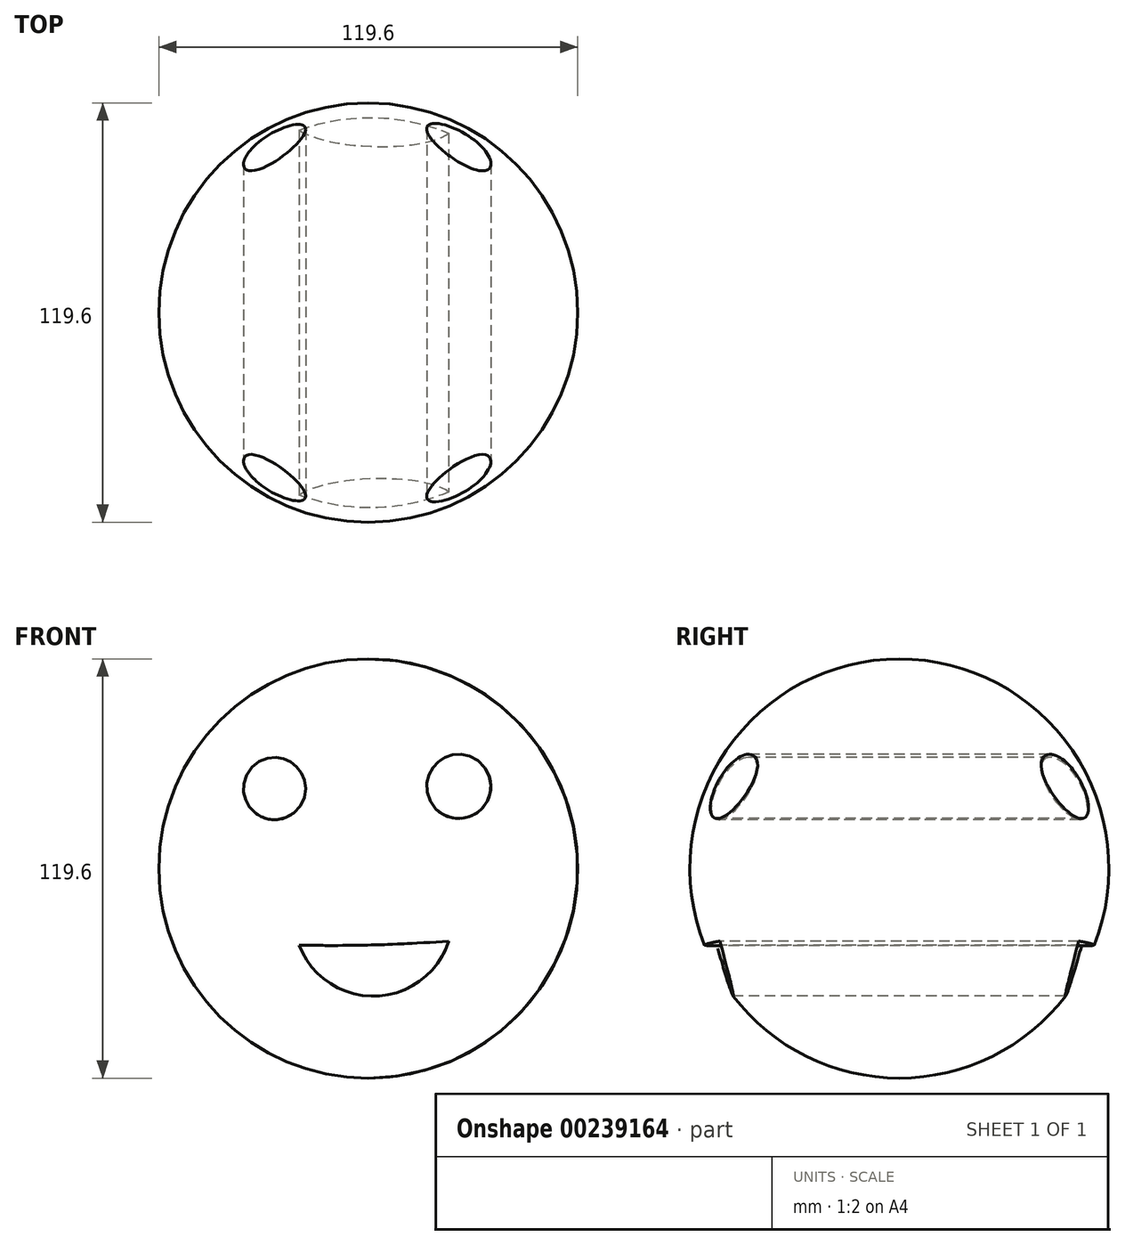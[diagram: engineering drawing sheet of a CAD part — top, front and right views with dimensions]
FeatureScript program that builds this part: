
annotation { "Feature Type Name" : "Feature", "Feature Type Description" : "" }
export const myFeature = defineFeature(function(context is Context, id is Id, definition is map)
    precondition{}
    {
        {
            var Q0;
            Q0=qCreatedBy(makeId("Front.planeOp"),FACE);
            var sketch = newSketch(context, id + "F0", { "sketchPlane" : qUnion([Q0])});
            skArc(sketch, "E0", {"start": v(0, -59.8) * mm, "mid": v(59.8, 0) * mm, "end": v(0, 59.8) * mm});
            skLineSegment(sketch, "E1", {"start": v(0, 59.8) * mm, "end": v(0, -59.8) * mm});
            skSolve(sketch);
        }
        {
            var Q0;
            Q0=makeQuery(id+"F0.imprint","IMPRINT",FACE,{"disambiguationData":[TD([[makeQuery(id+"F0.imprint","IMPRINT",EDGE,{"derivedFrom":sQuery(id+"F0.wireOp",EDGE,"E0")}),1.0]])]});
            var Q1;
            Q1=sQuery(id+"F0.wireOp",EDGE,"E1");
            revolve(context, id + "F1", {"entities" : qUnion([Q0]), "axis" : qUnion([Q1]), "revolveType" : RevolveType.FULL});
        }
        {
            var Q0;
            Q0=qCreatedBy(makeId("Front.planeOp"),FACE);
            var sketch = newSketch(context, id + "F2", { "sketchPlane" : qUnion([Q0])});
            skCircle(sketch, "E2", {"center": v(-26.74, 22.83) * mm, "radius": 8.88 * mm});
            skSolve(sketch);
        }
        {
            var Q0;
            Q0 = qSketchRegion(id + "F2", true);
            extrude(context, id + "F3", {"entities" : qUnion([Q0]), "operationType" : NewBodyOperationType.REMOVE, "endBound" : BoundingType.SYMMETRIC, "oppositeDirection" : true, "depth" : 197 * mm});
        }
        {
            var Q0;
            Q0=qCreatedBy(makeId("Front.planeOp"),FACE);
            var sketch = newSketch(context, id + "F4", { "sketchPlane" : qUnion([Q0])});
            skCircle(sketch, "E3", {"center": v(25.84, 23.44) * mm, "radius": 9.16 * mm});
            skSolve(sketch);
        }
        {
            var Q0;
            Q0 = qSketchRegion(id + "F4", true);
            extrude(context, id + "F5", {"entities" : qUnion([Q0]), "operationType" : NewBodyOperationType.REMOVE, "endBound" : BoundingType.SYMMETRIC, "oppositeDirection" : true, "depth" : 160.4 * mm});
        }
        {
            var Q0;
            Q0=qCreatedBy(makeId("Front.planeOp"),FACE);
            var sketch = newSketch(context, id + "F6", { "sketchPlane" : qUnion([Q0])});
            skArc(sketch, "E4", {"start": v(-19.7, -21.84) * mm, "mid": v(2.04, -36.4) * mm, "end": v(22.97, -20.69) * mm});
            skArc(sketch, "E5", {"start": v(-19.7, -21.84) * mm, "mid": v(1.65, -21.79) * mm, "end": v(22.97, -20.69) * mm});
            skSolve(sketch);
        }
        {
            var Q0;
            Q0 = qSketchRegion(id + "F6", true);
            extrude(context, id + "F7", {"entities" : qUnion([Q0]), "operationType" : NewBodyOperationType.REMOVE, "endBound" : BoundingType.SYMMETRIC, "oppositeDirection" : true, "depth" : 187 * mm});
        }
    });
